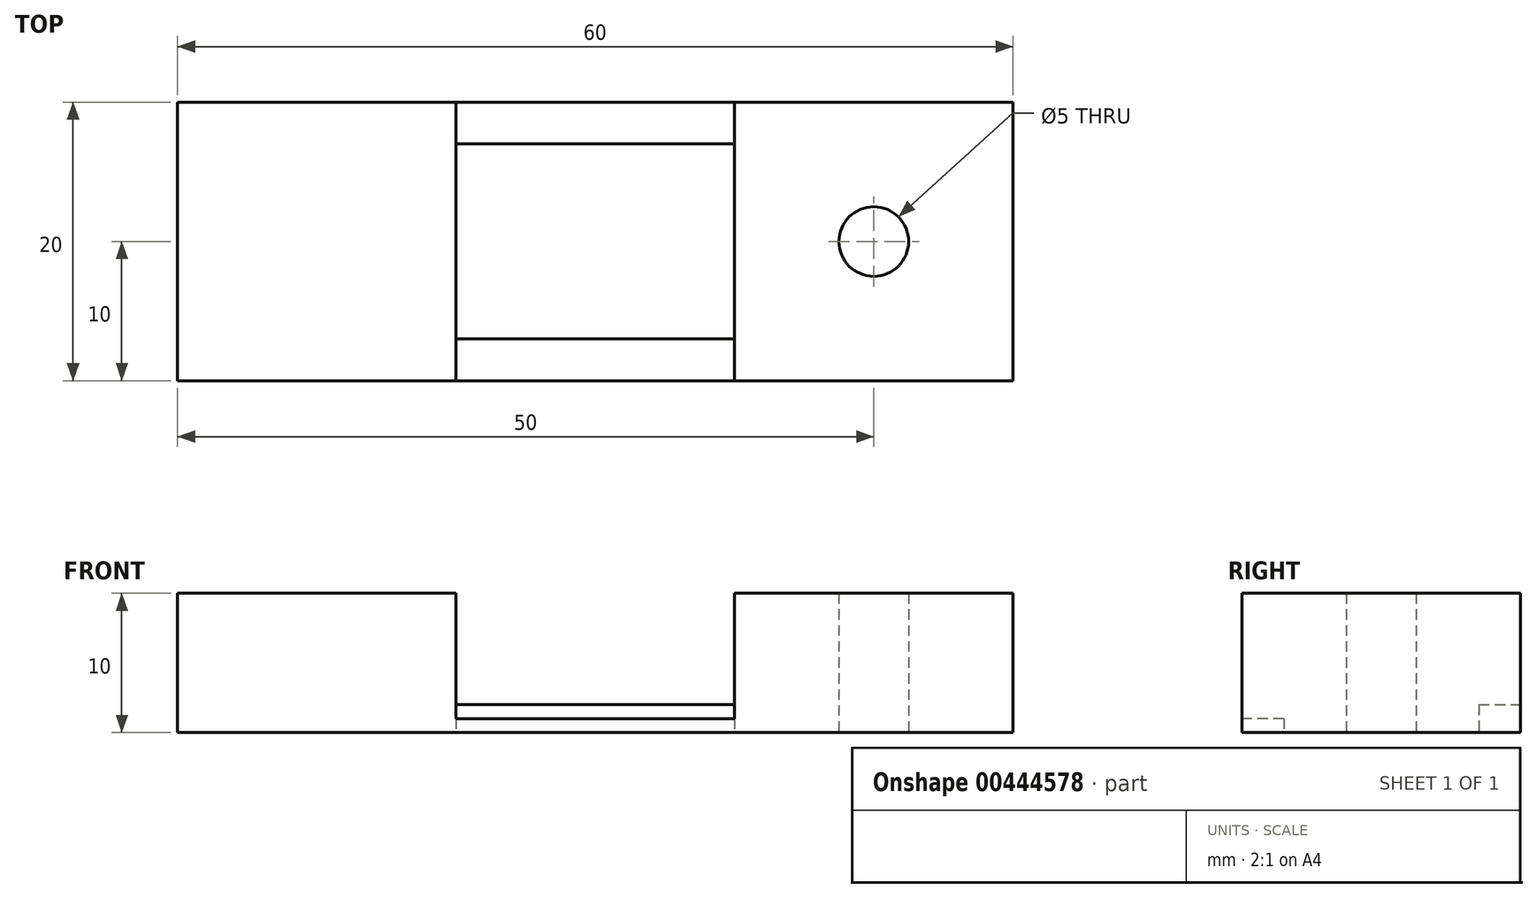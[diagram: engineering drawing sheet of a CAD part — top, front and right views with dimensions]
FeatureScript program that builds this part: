
annotation { "Feature Type Name" : "Feature", "Feature Type Description" : "" }
export const myFeature = defineFeature(function(context is Context, id is Id, definition is map)
    precondition{}
    {
        {
            var Q0;
            Q0=qCreatedBy(makeId("Top.planeOp"),FACE);
            var sketch = newSketch(context, id + "F0", { "sketchPlane" : qUnion([Q0])});
            skLineSegment(sketch, "E0.bottom", {"start": v(0, 0) * mm, "end": v(-20, 0) * mm});
            skLineSegment(sketch, "E0.top", {"start": v(0, 20) * mm, "end": v(-20, 20) * mm});
            skLineSegment(sketch, "E0.left", {"start": v(0, 0) * mm, "end": v(0, 20) * mm});
            skLineSegment(sketch, "E0.right", {"start": v(-20, 0) * mm, "end": v(-20, 20) * mm});
            skLineSegment(sketch, "E1.bottom", {"start": v(20, 0) * mm, "end": v(40, 0) * mm});
            skLineSegment(sketch, "E1.top", {"start": v(20, 20) * mm, "end": v(40, 20) * mm});
            skLineSegment(sketch, "E1.left", {"start": v(20, 0) * mm, "end": v(20, 20) * mm});
            skLineSegment(sketch, "E1.right", {"start": v(40, 0) * mm, "end": v(40, 20) * mm});
            skCircle(sketch, "E2", {"center": v(30, 10) * mm, "radius": 2.5 * mm});
            skSolve(sketch);
        }
        {
            var Q0;
            Q0=makeQuery(id+"F0.imprint","IMPRINT",FACE,{"disambiguationData":[TD([[makeQuery(id+"F0.imprint","IMPRINT",EDGE,{"derivedFrom":sQuery(id+"F0.wireOp",EDGE,"E0.bottom")}),-1.0]])]});
            var Q1;
            Q1=makeQuery(id+"F0.imprint","IMPRINT",FACE,{"disambiguationData":[TD([[makeQuery(id+"F0.imprint","IMPRINT",EDGE,{"derivedFrom":sQuery(id+"F0.wireOp",EDGE,"E1.bottom")}),1.0]])]});
            extrude(context, id + "F1", {"entities" : qUnion([Q0, Q1]), "depth" : 10 * mm});
        }
        {
            var Q0;
            Q0=makeQuery(id+"F1.opExtrude","SWEPT_FACE",FACE,{"disambiguationData":[OSD([sQuery(id+"F0.wireOp",EDGE,"E1.right")])]});
            var sketch = newSketch(context, id + "F2", { "sketchPlane" : qUnion([Q0])});
            skLineSegment(sketch, "E3.bottom", {"start": v(0, 0) * mm, "end": v(3, 0) * mm});
            skLineSegment(sketch, "E3.top", {"start": v(0, 1) * mm, "end": v(3, 1) * mm});
            skLineSegment(sketch, "E3.left", {"start": v(0, 0) * mm, "end": v(0, 1) * mm});
            skLineSegment(sketch, "E3.right", {"start": v(3, 0) * mm, "end": v(3, 1) * mm});
            skLineSegment(sketch, "E4.bottom", {"start": v(20, 0) * mm, "end": v(17, 0) * mm});
            skLineSegment(sketch, "E4.top", {"start": v(20, 2) * mm, "end": v(17, 2) * mm});
            skLineSegment(sketch, "E4.left", {"start": v(20, 0) * mm, "end": v(20, 2) * mm});
            skLineSegment(sketch, "E4.right", {"start": v(17, 0) * mm, "end": v(17, 2) * mm});
            skSolve(sketch);
        }
        {
            var Q0;
            Q0=makeQuery(id+"F2.imprint","IMPRINT",FACE,{"disambiguationData":[TD([[makeQuery(id+"F2.imprint","IMPRINT",EDGE,{"derivedFrom":sQuery(id+"F2.wireOp",EDGE,"E3.bottom")}),1.0]])]});
            var Q1;
            Q1=makeQuery(id+"F2.imprint","IMPRINT",FACE,{"disambiguationData":[TD([[makeQuery(id+"F2.imprint","IMPRINT",EDGE,{"derivedFrom":sQuery(id+"F2.wireOp",EDGE,"E4.bottom")}),1.0]])]});
            extrude(context, id + "F3", {"entities" : qUnion([Q0, Q1]), "operationType" : NewBodyOperationType.ADD, "oppositeDirection" : true, "depth" : 60 * mm});
        }
    });
